FCSTD DOCUMENT  (FreeCAD 0.19R24291 (Git))
Label: P12 orthographic
License: All rights reserved
LicenseURL: http://en.wikipedia.org/wiki/All_rights_reserved
objects: Part::Part2DObjectPython×28, App::FeaturePython×16
note: 28 computed .brp shape members not serialized (recipe doc carries the construction recipe); baked Part::Feature solids carry a one-line shape summary decoded from their .brp

FEATURE [Part::Part2DObjectPython] Line001  # Draft 2D object (typed FeaturePython)
  Area = 0
  ChamferSize = 0
  Closed = false
  End = (-30,30,0)
  FilletRadius = 0
  Length = 30
  MakeFace = false
  Placement = pos=(-30,-2.8e-15,0) rot=(0,0,1;0rad)
  Points = (2) [(0,0,0),(0,30,0)]
  Start = (-30,-2.8e-15,0)
  Subdivisions = 0
FEATURE [Part::Part2DObjectPython] Line002  # Draft 2D object (typed FeaturePython)
  Area = 0
  ChamferSize = 0
  Closed = false
  End = (0,30,0)
  FilletRadius = 0
  Length = 30
  MakeFace = false
  Points = (2) [(0,-2.75546e-15,0),(0,30,0)]
  Start = (0,-2.8e-15,0)
  Subdivisions = 0
FEATURE [Part::Part2DObjectPython] Line004  # Draft 2D object (typed FeaturePython)
  Area = 0
  ChamferSize = 0
  Closed = false
  End = (-30,10,0)
  FilletRadius = 0
  Length = 30
  MakeFace = false
  Points = (2) [(-6.12323e-16,10,0),(-30,10,0)]
  Start = (-6e-16,10,0)
  Subdivisions = 0
FEATURE [App::FeaturePython] Text  # WARN: FeaturePython — macro-defined, semantics opaque (R4)
  Placement = pos=(-34.153,-19.1257,0) rot=(0,0,1;0rad)
  Text = Right Side View
FEATURE [App::FeaturePython] Text001  # WARN: FeaturePython — macro-defined, semantics opaque (R4)
  Placement = pos=(46.6744,-21.248,0) rot=(0,0,1;0rad)
  Text = Front View
FEATURE [Part::Part2DObjectPython] Line  # Draft 2D object (typed FeaturePython)
  Area = 0
  ChamferSize = 0
  Closed = false
  End = (0,30,0)
  FilletRadius = 0
  Length = 30
  MakeFace = false
  Placement = pos=(-30,30,0) rot=(0,0,1;0rad)
  Points = (2) [(0,0,0),(30,0,0)]
  Start = (-30,30,0)
  Subdivisions = 0
FEATURE [Part::Part2DObjectPython] Line009  # Draft 2D object (typed FeaturePython)
  Area = 0
  ChamferSize = 0
  Closed = false
  End = (0,-2.8e-15,0)
  FilletRadius = 0
  Length = 30
  MakeFace = false
  Placement = pos=(-30,-2.8e-15,0) rot=(0,0,1;0rad)
  Points = (2) [(0,0,0),(30,-9.18485e-16,0)]
  Start = (-30,-2.8e-15,0)
  Subdivisions = 0
FEATURE [Part::Part2DObjectPython] Line010  # Draft 2D object (typed FeaturePython)
  Area = 0
  ChamferSize = 0
  Closed = false
  End = (82.9781,30,0)
  FilletRadius = 0
  Length = 45
  MakeFace = false
  Placement = pos=(37.9781,30,0) rot=(0,0,1;0rad)
  Points = (2) [(0,0,0),(45,-1.42109e-14,0)]
  Start = (37.9781,30,0)
  Subdivisions = 0
FEATURE [Part::Part2DObjectPython] Line014  # Draft 2D object (typed FeaturePython)
  Area = 0
  ChamferSize = 0
  Closed = false
  End = (42.9781,10,0)
  FilletRadius = 0
  Length = 35
  MakeFace = false
  Points = (2) [(77.9781,10,0),(42.9781,10,0)]
  Start = (77.9781,10,0)
  Subdivisions = 0
FEATURE [Part::Part2DObjectPython] Line015  # Draft 2D object (typed FeaturePython)
  Area = 0
  ChamferSize = 0
  Closed = false
  End = (0,17.5,0)
  FilletRadius = 0
  Length = 30
  MakeFace = false
  Points = (2) [(-30,17.5,0),(0,17.5,0)]
  Start = (-30,17.5,0)
  Subdivisions = 0
FEATURE [Part::Part2DObjectPython] Arc  # Draft 2D object (typed FeaturePython)
  Area = 0
  FirstAngle = -180
  LastAngle = 0
  MakeFace = false
  Placement = pos=(60.4781,30,0) rot=(0,0,1;0rad)
  Radius = 12.5
FEATURE [Part::Part2DObjectPython] Line016  # Draft 2D object (typed FeaturePython)
  Area = 0
  ChamferSize = 0
  Closed = false
  End = (42.9781,-1.8e-15,0)
  FilletRadius = 0
  Length = 10
  MakeFace = false
  Placement = pos=(42.9781,10,0) rot=(0,0,1;0rad)
  Points = (2) [(0,0,0),(0,-10,0)]
  Start = (42.9781,10,0)
  Subdivisions = 0
FEATURE [Part::Part2DObjectPython] Line017  # Draft 2D object (typed FeaturePython)
  Area = 0
  ChamferSize = 0
  Closed = false
  End = (77.9781,-1.8e-15,0)
  FilletRadius = 0
  Length = 10
  MakeFace = false
  Points = (2) [(77.9781,10,0),(77.9781,-1.77636e-15,0)]
  Start = (77.9781,10,0)
  Subdivisions = 0
FEATURE [Part::Part2DObjectPython] Line018  # Draft 2D object (typed FeaturePython)
  Area = 0
  ChamferSize = 0
  Closed = false
  End = (82.9781,-29.4922,0)
  FilletRadius = 0
  Length = 30
  MakeFace = false
  Placement = pos=(82.9781,-74.4922,0) rot=(0,0,1;1.5708rad)
  Points = (2) [(15,0,0),(45,0,0)]
  Start = (82.9781,-59.4922,0)
  Subdivisions = 0
FEATURE [Part::Part2DObjectPython] Line019  # Draft 2D object (typed FeaturePython)
  Area = 0
  ChamferSize = 0
  Closed = false
  End = (37.9781,-29.4922,0)
  FilletRadius = 0
  Length = 30
  MakeFace = false
  Placement = pos=(8.48591,-112.47,0) rot=(0,0,1;1.5708rad)
  Points = (2) [(52.9781,-29.4922,0),(82.9781,-29.4922,0)]
  Start = (37.9781,-59.4922,0)
  Subdivisions = 0
FEATURE [Part::Part2DObjectPython] Line020  # Draft 2D object (typed FeaturePython)
  Area = 0
  ChamferSize = 0
  Closed = false
  End = (47.9781,-29.4922,0)
  FilletRadius = 0
  Length = 30
  MakeFace = false
  Placement = pos=(8.48591,-112.47,0) rot=(0,0,1;1.5708rad)
  Points = (2) [(52.9781,-39.4922,0),(82.9781,-39.4922,0)]
  Start = (47.9781,-59.4922,0)
  Subdivisions = 0
FEATURE [Part::Part2DObjectPython] Line021  # Draft 2D object (typed FeaturePython)
  Area = 0
  ChamferSize = 0
  Closed = false
  End = (72.9781,-29.4922,0)
  FilletRadius = 0
  Length = 30
  MakeFace = false
  Placement = pos=(8.48591,-112.47,0) rot=(0,0,1;1.5708rad)
  Points = (2) [(52.9781,-64.4922,0),(82.9781,-64.4922,0)]
  Start = (72.9781,-59.4922,0)
  Subdivisions = 0
FEATURE [Part::Part2DObjectPython] Line022  # Draft 2D object (typed FeaturePython)
  Area = 0
  ChamferSize = 0
  Closed = false
  End = (42.9781,-29.4922,0)
  FilletRadius = 0
  Length = 30
  MakeFace = false
  Placement = pos=(8.48591,-112.47,0) rot=(0,0,1;1.5708rad)
  Points = (2) [(52.9781,-34.4922,0),(82.9781,-34.4922,0)]
  Start = (42.9781,-59.4922,0)
  Subdivisions = 0
FEATURE [Part::Part2DObjectPython] Line023  # Draft 2D object (typed FeaturePython)
  Area = 0
  ChamferSize = 0
  Closed = false
  End = (77.9781,-29.4922,0)
  FilletRadius = 0
  Length = 30
  MakeFace = false
  Placement = pos=(8.48591,-112.47,0) rot=(0,0,1;1.5708rad)
  Points = (2) [(52.9781,-69.4922,0),(82.9781,-69.4922,0)]
  Start = (77.9781,-59.4922,0)
  Subdivisions = 0
FEATURE [Part::Part2DObjectPython] Line025  # Draft 2D object (typed FeaturePython)
  Area = 0
  ChamferSize = 0
  Closed = false
  End = (82.9781,0,0)
  FilletRadius = 0
  Length = 30
  MakeFace = false
  Placement = pos=(82.9781,30,0) rot=(0,0,1;0rad)
  Points = (2) [(0,0,0),(0,-30,0)]
  Start = (82.9781,30,0)
  Subdivisions = 0
FEATURE [Part::Part2DObjectPython] Line026  # Draft 2D object (typed FeaturePython)
  Area = 0
  ChamferSize = 0
  Closed = false
  End = (37.9781,-3.6e-15,0)
  FilletRadius = 0
  Length = 30
  MakeFace = false
  Placement = pos=(37.9781,30,0) rot=(0,0,1;0rad)
  Points = (2) [(0,0,0),(0,-30,0)]
  Start = (37.9781,30,0)
  Subdivisions = 0
FEATURE [Part::Part2DObjectPython] Line027  # Draft 2D object (typed FeaturePython)
  Area = 0
  ChamferSize = 0
  Closed = false
  End = (82.9781,-29.4922,0)
  FilletRadius = 0
  Length = 45
  MakeFace = false
  Placement = pos=(37.9781,-29.4922,0) rot=(0,0,1;0rad)
  Points = (2) [(0,0,0),(45,-8.52651e-14,0)]
  Start = (37.9781,-29.4922,0)
  Subdivisions = 0
FEATURE [Part::Part2DObjectPython] Line028  # Draft 2D object (typed FeaturePython)
  Area = 0
  ChamferSize = 0
  Closed = false
  End = (37.9781,30,0)
  FilletRadius = 0
  Length = 37.9781
  MakeFace = false
  Placement = pos=(0,30,0) rot=(0,0,1;0rad)
  Points = (2) [(0,0,0),(37.9781,0,0)]
  Start = (0,30,0)
  Subdivisions = 0
FEATURE [Part::Part2DObjectPython] Line029  # Draft 2D object (typed FeaturePython)
  Area = 0
  ChamferSize = 0
  Closed = false
  End = (37.9781,-3.6e-15,0)
  FilletRadius = 0
  Length = 37.9781
  MakeFace = false
  Placement = pos=(0,-2.8e-15,0) rot=(0,0,1;0rad)
  Points = (2) [(0,0,0),(37.9781,-1.96e-15,0)]
  Start = (0,-2.8e-15,0)
  Subdivisions = 0
FEATURE [Part::Part2DObjectPython] Line030  # Draft 2D object (typed FeaturePython)
  Area = 0
  ChamferSize = 0
  Closed = false
  End = (37.9781,-29.4922,0)
  FilletRadius = 0
  Length = 29.4922
  MakeFace = false
  Placement = pos=(37.9781,-2.8e-15,0) rot=(0,0,1;0rad)
  Points = (2) [(0,0,0),(7.10543e-15,-29.4922,0)]
  Start = (37.9781,-2.8e-15,0)
  Subdivisions = 0
FEATURE [Part::Part2DObjectPython] Line031  # Draft 2D object (typed FeaturePython)
  Area = 0
  ChamferSize = 0
  Closed = false
  End = (82.9781,-29.4922,0)
  FilletRadius = 0
  Length = 44.4922
  MakeFace = false
  Placement = pos=(82.9781,15,0) rot=(0,0,1;0rad)
  Points = (2) [(0,0,0),(-8.52651e-14,-44.4922,0)]
  Start = (82.9781,15,0)
  Subdivisions = 0
FEATURE [App::FeaturePython] Dimension  # Draft dimension (typed FeaturePython)
  Diameter = false
  Dimline = (-47.1651,1.55665,0)
  Direction = (0,0,0)
  Distance = 30
  End = (-30,-2.8e-15,0)
  Normal = (0,0,1)
  Start = (-30,30,0)
FEATURE [App::FeaturePython] Dimension001  # Draft dimension (typed FeaturePython)
  Diameter = false
  Dimline = (-35,-3.1e-15,0)
  Direction = (0,0,0)
  Distance = 10
  End = (-30,-2.8e-15,0)
  Normal = (0,0,1)
  Start = (-30,10,0)
FEATURE [App::FeaturePython] Dimension002  # Draft dimension (typed FeaturePython)
  Diameter = false
  Dimline = (-30,-4,0)
  Direction = (0,0,0)
  Distance = 30
  End = (-30,-2.8e-15,0)
  Normal = (0,0,1)
  Start = (0,-2.8e-15,0)
FEATURE [App::FeaturePython] Dimension004  # Draft dimension (typed FeaturePython)
  Diameter = false
  Dimline = (42.9781,-4,0)
  Direction = (0,0,0)
  Distance = 5
  End = (42.9781,-1.8e-15,0)
  Normal = (0,0,1)
  Start = (37.9781,-3.6e-15,0)
FEATURE [App::FeaturePython] Dimension005  # Draft dimension (typed FeaturePython)
  Diameter = false
  Dimline = (70.2441,-12.7341,0)
  Direction = (0,0,0)
  Distance = 45
  End = (82.9781,0,0)
  Normal = (0,0,1)
  Start = (37.9781,-2.8e-15,0)
FEATURE [App::FeaturePython] Dimension007  # Draft dimension (typed FeaturePython)
  Diameter = false
  Dimline = (37.9781,34,0)
  Direction = (0,0,0)
  Distance = 10
  End = (37.9781,30,0)
  Normal = (0,0,1)
  Start = (47.9781,30,0)
FEATURE [App::FeaturePython] Dimension008  # Draft dimension (typed FeaturePython)
  Diameter = false
  Dimline = (82.9781,34,0)
  Direction = (0,0,0)
  Distance = 10
  End = (82.9781,30,0)
  Normal = (0,0,1)
  Start = (72.9781,30,0)
FEATURE [App::FeaturePython] Dimension010  # Draft dimension (typed FeaturePython)
  Diameter = false
  Dimline = (90.9781,5e-16,0)
  Direction = (0,0,0)
  Distance = 30
  End = (82.9781,0,0)
  Normal = (0,0,1)
  Start = (82.9781,30,0)
FEATURE [Part::Part2DObjectPython] Line032  # Draft 2D object (typed FeaturePython)
  Area = 0
  ChamferSize = 0
  Closed = false
  End = (42.9781,-2.4e-15,0)
  FilletRadius = 0
  Length = 5
  MakeFace = false
  Placement = pos=(37.9781,-4e-15,0) rot=(0,0,1;0rad)
  Points = (2) [(0,0,0),(5,1.62328e-15,0)]
  Start = (37.9781,-4e-15,0)
  Subdivisions = 0
FEATURE [Part::Part2DObjectPython] Line033  # Draft 2D object (typed FeaturePython)
  Area = 0
  ChamferSize = 0
  Closed = false
  End = (82.9781,0,0)
  FilletRadius = 0
  Length = 5
  MakeFace = false
  Placement = pos=(77.9781,-1.8e-15,0) rot=(0,0,1;0rad)
  Points = (2) [(0,0,0),(5,1.62328e-15,0)]
  Start = (77.9781,-1.8e-15,0)
  Subdivisions = 0
FEATURE [Part::Part2DObjectPython] Line034  # Draft 2D object (typed FeaturePython)
  Area = 0
  ChamferSize = 0
  Closed = false
  End = (82.9781,-59.4922,0)
  FilletRadius = 0
  Length = 45
  MakeFace = false
  Points = (2) [(37.9781,-59.4922,0),(82.9781,-59.4922,0)]
  Start = (37.9781,-59.4922,0)
  Subdivisions = 0
FEATURE [App::FeaturePython] Dimension011  # Draft dimension (typed FeaturePython)
  Diameter = false
  Dimline = (90.9781,-59.4922,0)
  Direction = (0,0,0)
  Distance = 30
  End = (82.9781,-59.4922,0)
  Normal = (0,0,1)
  Start = (82.9781,-29.4922,0)
FEATURE [App::FeaturePython] Dimension012  # Draft dimension (typed FeaturePython)
  Diameter = false
  Dimline = (82.9781,-66.3709,0)
  Direction = (0,0,0)
  Distance = 45
  End = (82.9781,-59.4922,0)
  Normal = (0,0,1)
  Start = (37.9781,-59.4922,0)
FEATURE [App::FeaturePython] Text002  # WARN: FeaturePython — macro-defined, semantics opaque (R4)
  Placement = pos=(50.2986,-77.3835,0) rot=(0,0,1;0rad)
  Text = Top View
FEATURE [App::FeaturePython] Dimension013  # Draft dimension (typed FeaturePython)
  Diameter = false
  Dimline = (51.179,1.82951,0)
  Direction = (0,0,0)
  Distance = 10
  End = (42.9781,-1.8e-15,0)
  Normal = (0,0,1)
  Start = (42.9781,10,0)
FEATURE [App::FeaturePython] Dimension014  # Draft dimension (typed FeaturePython)
  Diameter = false
  Dimline = (41.1927,-4.08072,0)
  Direction = (0,0,0)
  Distance = 4.38242
  End = (82.3606,-1.5e-15,0)
  Normal = (0,0,1)
  Start = (77.9781,-1.8e-15,0)
FEATURE [Part::Part2DObjectPython] Line035  # Draft 2D object (typed FeaturePython)
  Area = 0
  ChamferSize = 0
  Closed = false
  End = (60.4781,-59.4922,0)
  FilletRadius = 0
  Length = 30
  MakeFace = false
  Placement = pos=(60.4781,-29.4922,0) rot=(0,0,1;0rad)
  Points = (2) [(0,0,0),(0,-30,0)]
  Start = (60.4781,-29.4922,0)
  Subdivisions = 0
FEATURE [App::FeaturePython] Text003  # WARN: FeaturePython — macro-defined, semantics opaque (R4)
  Placement = pos=(-11.297,-90.0268,0) rot=(0,0,1;0rad)
  Text = All Dimensions are in mm
